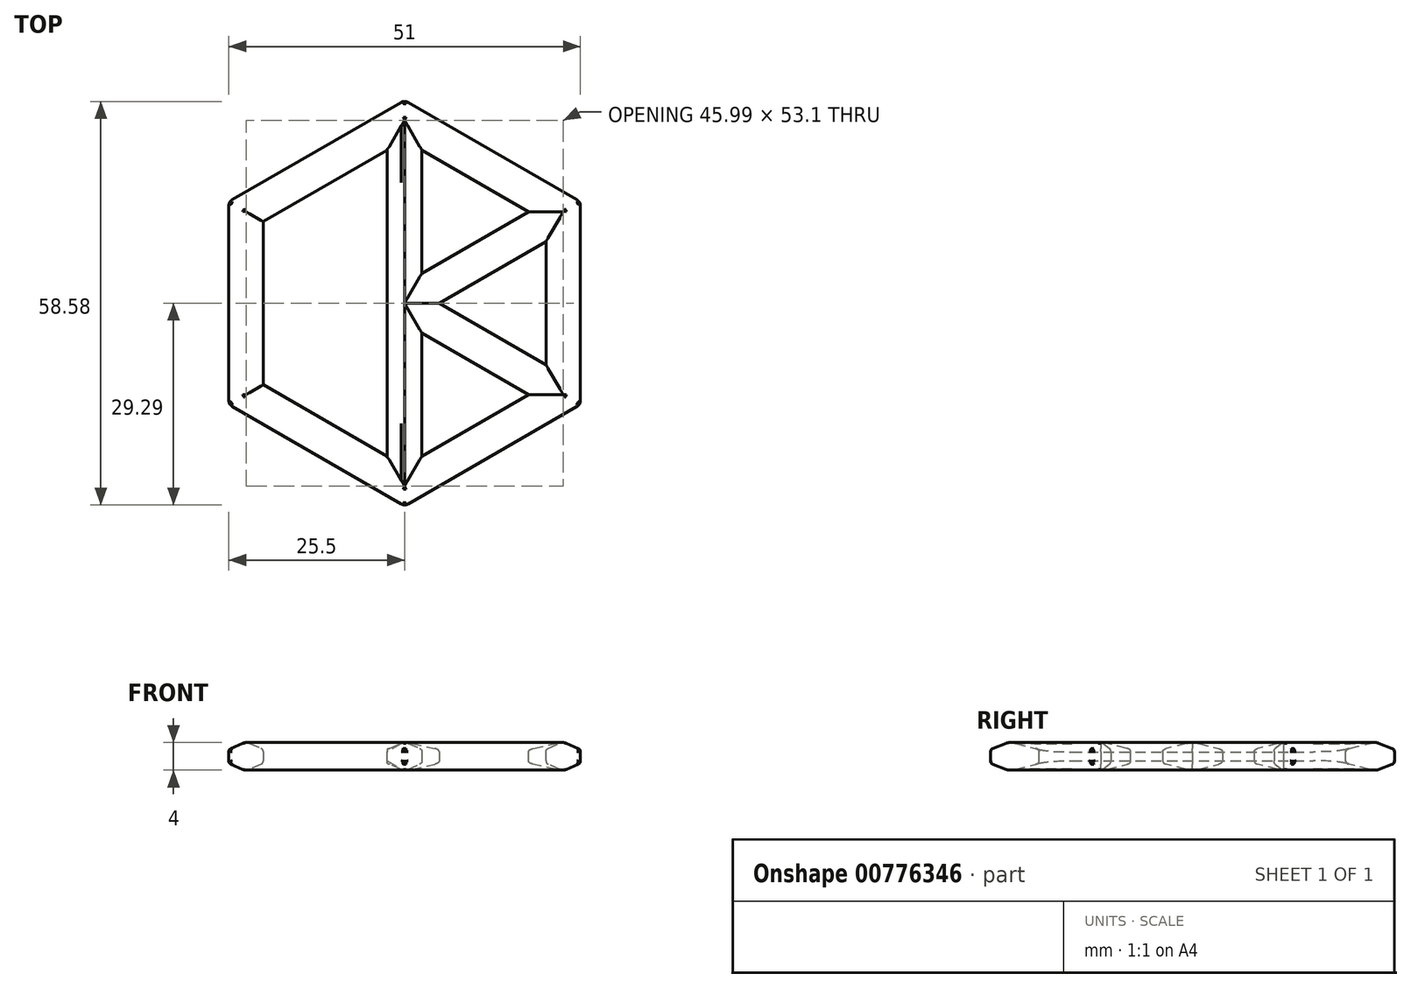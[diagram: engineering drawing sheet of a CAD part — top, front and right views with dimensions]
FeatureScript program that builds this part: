
annotation { "Feature Type Name" : "Feature", "Feature Type Description" : "" }
export const myFeature = defineFeature(function(context is Context, id is Id, definition is map)
    precondition{}
    {
        {
            var Q0;
            Q0=qCreatedBy(makeId("Top.planeOp"),FACE);
            var sketch = newSketch(context, id + "F0", { "sketchPlane" : qUnion([Q0])});
            skCircle(sketch, "E0.cCircle", {"center": v(0, 0) * mm, "radius": 25.5 * mm, "construction": true});
            skLineSegment(sketch, "E0.0", {"start": v(-25.5, -14.72) * mm, "end": v(-25.5, 14.72) * mm});
            skLineSegment(sketch, "E0.1", {"start": v(-25.5, 14.72) * mm, "end": v(0, 29.44) * mm});
            skLineSegment(sketch, "E0.2", {"start": v(0, 29.44) * mm, "end": v(25.5, 14.72) * mm});
            skLineSegment(sketch, "E0.3", {"start": v(25.5, 14.72) * mm, "end": v(25.5, -14.72) * mm});
            skLineSegment(sketch, "E0.4", {"start": v(25.5, -14.72) * mm, "end": v(0, -29.44) * mm});
            skLineSegment(sketch, "E0.5", {"start": v(0, -29.44) * mm, "end": v(-25.5, -14.72) * mm});
            skPoint(sketch, "E0.0.midPoint", {"position": v(-25.5, 0) * mm});
            skSolve(sketch);
        }
        {
            var Q0;
            Q0=qCreatedBy(makeId("Front.planeOp"),FACE);
            var sketch = newSketch(context, id + "F1", { "sketchPlane" : qUnion([Q0])});
            skLineSegment(sketch, "E1", {"start": v(-25.5, -1) * mm, "end": v(-25.5, 1) * mm});
            skLineSegment(sketch, "E2", {"start": v(-22.75, 2) * mm, "end": v(-20.5, 1) * mm});
            skLineSegment(sketch, "E3", {"start": v(-20.5, 1) * mm, "end": v(-20.5, -1) * mm});
            skLineSegment(sketch, "E4", {"start": v(-20.5, -1) * mm, "end": v(-22.75, -2) * mm});
            skLineSegment(sketch, "E5", {"start": v(-23.25, 2) * mm, "end": v(-23.25, -2) * mm});
            skLineSegment(sketch, "E6", {"start": v(-22.75, -2) * mm, "end": v(-22.75, 2) * mm});
            skLineSegment(sketch, "E7", {"start": v(-25.5, -1) * mm, "end": v(-23.25, -2) * mm});
            skLineSegment(sketch, "E8", {"start": v(-22.75, -2) * mm, "end": v(-23.25, -2) * mm});
            skLineSegment(sketch, "E9", {"start": v(-23.25, 2) * mm, "end": v(-22.75, 2) * mm});
            skLineSegment(sketch, "E10", {"start": v(-25.5, 1) * mm, "end": v(-23.25, 2) * mm});
            skLineSegment(sketch, "E11", {"start": v(-22.75, 2) * mm, "end": v(-23.25, -2) * mm});
            skPoint(sketch, "E12", {"position": v(-23, 0) * mm});
            skSolve(sketch);
        }
        {
            var Q0;
            Q0=makeQuery(id+"F1.imprint","IMPRINT",FACE,{"disambiguationData":[TD([[makeQuery(id+"F1.imprint","IMPRINT",EDGE,{"derivedFrom":sQuery(id+"F1.wireOp",EDGE,"E1")}),-1.0]])]});
            var Q1;
            Q1=makeQuery(id+"F1.imprint","IMPRINT",FACE,{"disambiguationData":[TD([[makeQuery(id+"F1.imprint","IMPRINT",EDGE,{"derivedFrom":sQuery(id+"F1.wireOp",EDGE,"E5")}),1.0]])]});
            var Q2;
            Q2=makeQuery(id+"F1.imprint","IMPRINT",FACE,{"disambiguationData":[TD([[makeQuery(id+"F1.imprint","IMPRINT",EDGE,{"derivedFrom":sQuery(id+"F1.wireOp",EDGE,"E6")}),1.0]])]});
            var Q3;
            Q3=makeQuery(id+"F1.imprint","IMPRINT",FACE,{"disambiguationData":[TD([[makeQuery(id+"F1.imprint","IMPRINT",EDGE,{"derivedFrom":sQuery(id+"F1.wireOp",EDGE,"E2")}),-1.0]])]});
            var Q4;
            Q4=sQuery(id+"F0.wireOp",EDGE,"E0.3");
            var Q5;
            Q5=sQuery(id+"F0.wireOp",EDGE,"E0.2");
            var Q6;
            Q6=sQuery(id+"F0.wireOp",EDGE,"E0.1");
            var Q7;
            Q7=sQuery(id+"F0.wireOp",EDGE,"E0.0");
            var Q8;
            Q8=sQuery(id+"F0.wireOp",EDGE,"E0.5");
            var Q9;
            Q9=sQuery(id+"F0.wireOp",EDGE,"E0.4");
            sweep(context, id + "F2", {"profiles" : qUnion([Q0, Q1, Q2, Q3]), "path" : qUnion([Q4, Q5, Q6, Q7, Q8, Q9])});
        }
        {
            var Q0;
            Q0=qCreatedBy(makeId("Front.planeOp"),FACE);
            var sketch = newSketch(context, id + "F3", { "sketchPlane" : qUnion([Q0])});
            skLineSegment(sketch, "E13", {"start": v(-2.5, -1) * mm, "end": v(-2.5, 1) * mm});
            skLineSegment(sketch, "E14", {"start": v(0.25, 2) * mm, "end": v(2.5, 1) * mm});
            skLineSegment(sketch, "E15", {"start": v(2.5, 1) * mm, "end": v(2.5, -1) * mm});
            skLineSegment(sketch, "E16", {"start": v(2.5, -1) * mm, "end": v(0.25, -2) * mm});
            skLineSegment(sketch, "E17", {"start": v(-0.25, 2) * mm, "end": v(-0.25, -2) * mm});
            skLineSegment(sketch, "E18", {"start": v(0.25, -2) * mm, "end": v(0.25, 2) * mm});
            skLineSegment(sketch, "E19", {"start": v(-2.5, -1) * mm, "end": v(-0.25, -2) * mm});
            skLineSegment(sketch, "E20", {"start": v(0.25, -2) * mm, "end": v(-0.25, -2) * mm});
            skLineSegment(sketch, "E21", {"start": v(-0.25, 2) * mm, "end": v(0.25, 2) * mm});
            skLineSegment(sketch, "E22", {"start": v(-2.5, 1) * mm, "end": v(-0.25, 2) * mm});
            skLineSegment(sketch, "E23", {"start": v(0, 2) * mm, "end": v(0, -2) * mm});
            skPoint(sketch, "E24", {"position": v(0, 0) * mm});
            skSolve(sketch);
        }
        {
            var Q0;
            Q0 = qSketchRegion(id + "F3", true);
            extrude(context, id + "F4", {"entities" : qUnion([Q0]), "endBound" : BoundingType.UP_TO_NEXT, "depth" : 25 * mm, "offsetDistance" : 25 * mm});
        }
        {
            var Q0;
            Q0=makeQuery(id+"F4.opExtrude","SWEPT_BODY",BODY,{"disambiguationData":[OSD([sQuery(id+"F3.wireOp",EDGE,"E13"),sQuery(id+"F3.wireOp",EDGE,"E14"),sQuery(id+"F3.wireOp",EDGE,"E15"),sQuery(id+"F3.wireOp",EDGE,"E16"),sQuery(id+"F3.wireOp",EDGE,"E19"),sQuery(id+"F3.wireOp",EDGE,"E20"),sQuery(id+"F3.wireOp",EDGE,"E21"),sQuery(id+"F3.wireOp",EDGE,"E22")])]});
            var Q1;
            Q1=sQuery(id+"F3.wireOp",EDGE,"E23");
            circularPattern(context, id + "F5", {"operationType" : NewBodyOperationType.ADD, "entities" : qUnion([Q0]), "axis" : qUnion([Q1]), "angle" : 180 * degree, "instanceCount" : 4, "oppositeDirection" : true, "equalSpace" : true});
        }
        {
            var Q0;
            Q0=qCreatedBy(makeId("Top.planeOp"),FACE);
            var sketch = newSketch(context, id + "F6", { "sketchPlane" : qUnion([Q0])});
            skLineSegment(sketch, "E25", {"start": v(-2.5, 22.23) * mm, "end": v(-0.25, 26.13) * mm});
            skLineSegment(sketch, "E26", {"start": v(-0.25, 26.13) * mm, "end": v(-0.25, -26.13) * mm});
            skLineSegment(sketch, "E27", {"start": v(-0.25, -26.13) * mm, "end": v(-2.5, -22.23) * mm});
            skLineSegment(sketch, "E28", {"start": v(-2.5, -22.23) * mm, "end": v(-2.5, 22.23) * mm});
            skSolve(sketch);
        }
        {
            var Q0;
            Q0 = qSketchRegion(id + "F6", true);
            extrude(context, id + "F7", {"entities" : qUnion([Q0]), "operationType" : NewBodyOperationType.REMOVE, "endBound" : BoundingType.SYMMETRIC, "oppositeDirection" : true, "depth" : 5 * mm, "offsetDistance" : 25 * mm});
        }
        {
            var Q0;
            Q0=qCreatedBy(makeId("Front.planeOp"),FACE);
            var sketch = newSketch(context, id + "F8", { "sketchPlane" : qUnion([Q0])});
            skLineSegment(sketch, "E29", {"start": v(-0.25, 2) * mm, "end": v(-2.5, 0.65) * mm});
            skLineSegment(sketch, "E30", {"start": v(-2.5, 0.65) * mm, "end": v(-2.5, -0.65) * mm});
            skLineSegment(sketch, "E31", {"start": v(-2.5, -0.65) * mm, "end": v(-0.25, -2) * mm});
            skLineSegment(sketch, "E32", {"start": v(-0.25, -2) * mm, "end": v(-0.25, 2) * mm});
            skSolve(sketch);
        }
        {
            var Q0;
            Q0 = qSketchRegion(id + "F8", true);
            extrude(context, id + "F9", {"entities" : qUnion([Q0]), "operationType" : NewBodyOperationType.ADD, "endBound" : BoundingType.SYMMETRIC, "depth" : 35 * mm, "offsetDistance" : 25 * mm});
        }
        {
            var Q1;
            Q1=makeQuery(id+"F7.boolean.opBoolean","COPY",FACE,{"derivedFrom":makeQuery(id+"F7.opExtrude","SWEPT_FACE",FACE,{"disambiguationData":[OSD([sQuery(id+"F6.wireOp",EDGE,"E25")])]})});
            var Q2;
            Q2=makeQuery(id+"F9.opExtrude","CAP_FACE",FACE,{"disambiguationData":[OSD([sQuery(id+"F8.wireOp",EDGE,"E29"),sQuery(id+"F8.wireOp",EDGE,"E30"),sQuery(id+"F8.wireOp",EDGE,"E31"),sQuery(id+"F8.wireOp",EDGE,"E32")])],"isStart":true});
            loft(context, id + "F10", {"operationType" : NewBodyOperationType.ADD, "endCondition" : LoftEndDerivativeType.MATCH_TANGENT, "endMagnitude" : 2, "sheetProfilesArray" : [{ "sheetProfileEntities" : qUnion([Q1]) }, { "sheetProfileEntities" : qUnion([Q2]) }]});
        }
        {
            var Q1;
            Q1=makeQuery(id+"F7.boolean.opBoolean","COPY",FACE,{"derivedFrom":makeQuery(id+"F7.opExtrude","SWEPT_FACE",FACE,{"disambiguationData":[OSD([sQuery(id+"F6.wireOp",EDGE,"E27")])]})});
            var Q2;
            Q2=makeQuery(id+"F9.opExtrude","CAP_FACE",FACE,{"disambiguationData":[OSD([sQuery(id+"F8.wireOp",EDGE,"E29"),sQuery(id+"F8.wireOp",EDGE,"E30"),sQuery(id+"F8.wireOp",EDGE,"E31"),sQuery(id+"F8.wireOp",EDGE,"E32")])],"isStart":false});
            loft(context, id + "F11", {"operationType" : NewBodyOperationType.ADD, "endCondition" : LoftEndDerivativeType.MATCH_TANGENT, "endMagnitude" : 2, "sheetProfilesArray" : [{ "sheetProfileEntities" : qUnion([Q1]) }, { "sheetProfileEntities" : qUnion([Q2]) }]});
        }
        {
            var Q0;
            Q0=makeQuery(id+"F2.opSweep","MID_CAP_EDGE",EDGE,{"disambiguationData":[OSD([sQuery(id+"F0.wireOp",VERTEX,"E0.4.start"),sQuery(id+"F1.wireOp",EDGE,"E1")])],"capPos":2.0});
            var Q1;
            Q1=makeQuery(id+"F2.opSweep","MID_CAP_EDGE",EDGE,{"disambiguationData":[OSD([sQuery(id+"F0.wireOp",VERTEX,"E0.4.start"),sQuery(id+"F1.wireOp",EDGE,"E10")])],"capPos":2.0});
            var Q2;
            Q2=makeQuery(id+"F2.opSweep","MID_CAP_EDGE",EDGE,{"disambiguationData":[OSD([sQuery(id+"F0.wireOp",VERTEX,"E0.4.start"),sQuery(id+"F1.wireOp",EDGE,"E7")])],"capPos":2.0});
            var Q3;
            Q3=makeQuery(id+"F2.opSweep","MID_CAP_EDGE",EDGE,{"disambiguationData":[OSD([sQuery(id+"F0.wireOp",VERTEX,"E0.2.end"),sQuery(id+"F1.wireOp",EDGE,"E10")])],"capPos":3.0});
            var Q4;
            Q4=makeQuery(id+"F2.opSweep","MID_CAP_EDGE",EDGE,{"disambiguationData":[OSD([sQuery(id+"F0.wireOp",VERTEX,"E0.2.end"),sQuery(id+"F1.wireOp",EDGE,"E1")])],"capPos":3.0});
            var Q5;
            Q5=makeQuery(id+"F2.opSweep","MID_CAP_EDGE",EDGE,{"disambiguationData":[OSD([sQuery(id+"F0.wireOp",VERTEX,"E0.2.end"),sQuery(id+"F1.wireOp",EDGE,"E7")])],"capPos":3.0});
            var Q6;
            Q6=makeQuery(id+"F2.opSweep","MID_CAP_EDGE",EDGE,{"disambiguationData":[OSD([sQuery(id+"F0.wireOp",VERTEX,"E0.1.end"),sQuery(id+"F1.wireOp",EDGE,"E7")])],"capPos":4.0});
            var Q7;
            Q7=makeQuery(id+"F2.opSweep","MID_CAP_EDGE",EDGE,{"disambiguationData":[OSD([sQuery(id+"F0.wireOp",VERTEX,"E0.1.end"),sQuery(id+"F1.wireOp",EDGE,"E1")])],"capPos":4.0});
            var Q8;
            Q8=makeQuery(id+"F2.opSweep","MID_CAP_EDGE",EDGE,{"disambiguationData":[OSD([sQuery(id+"F0.wireOp",VERTEX,"E0.1.end"),sQuery(id+"F1.wireOp",EDGE,"E10")])],"capPos":4.0});
            var Q9;
            Q9=makeQuery(id+"F2.opSweep","MID_CAP_EDGE",EDGE,{"disambiguationData":[OSD([sQuery(id+"F0.wireOp",VERTEX,"E0.0.end"),sQuery(id+"F1.wireOp",EDGE,"E1")])],"capPos":5.0});
            var Q10;
            Q10=makeQuery(id+"F2.opSweep","MID_CAP_EDGE",EDGE,{"disambiguationData":[OSD([sQuery(id+"F0.wireOp",VERTEX,"E0.0.end"),sQuery(id+"F1.wireOp",EDGE,"E10")])],"capPos":5.0});
            var Q11;
            Q11=makeQuery(id+"F2.opSweep","MID_CAP_EDGE",EDGE,{"disambiguationData":[OSD([sQuery(id+"F0.wireOp",VERTEX,"E0.0.end"),sQuery(id+"F1.wireOp",EDGE,"E7")])],"capPos":5.0});
            var Q12;
            Q12=makeQuery(id+"F2.opSweep","CAP_EDGE",EDGE,{"disambiguationData":[OSD([sQuery(id+"F0.wireOp",VERTEX,"E0.5.end"),sQuery(id+"F1.wireOp",EDGE,"E7")])],"isStart":true});
            var Q13;
            Q13=makeQuery(id+"F2.opSweep","CAP_EDGE",EDGE,{"disambiguationData":[OSD([sQuery(id+"F0.wireOp",VERTEX,"E0.5.end"),sQuery(id+"F1.wireOp",EDGE,"E1")])],"isStart":true});
            var Q14;
            Q14=makeQuery(id+"F2.opSweep","CAP_EDGE",EDGE,{"disambiguationData":[OSD([sQuery(id+"F0.wireOp",VERTEX,"E0.5.end"),sQuery(id+"F1.wireOp",EDGE,"E10")])],"isStart":true});
            var Q15;
            Q15=makeQuery(id+"F2.opSweep","MID_CAP_EDGE",EDGE,{"disambiguationData":[OSD([sQuery(id+"F0.wireOp",VERTEX,"E0.4.end"),sQuery(id+"F1.wireOp",EDGE,"E10")])],"capPos":1.0});
            var Q16;
            Q16=makeQuery(id+"F2.opSweep","MID_CAP_EDGE",EDGE,{"disambiguationData":[OSD([sQuery(id+"F0.wireOp",VERTEX,"E0.4.end"),sQuery(id+"F1.wireOp",EDGE,"E1")])],"capPos":1.0});
            var Q17;
            Q17=makeQuery(id+"F2.opSweep","MID_CAP_EDGE",EDGE,{"disambiguationData":[OSD([sQuery(id+"F0.wireOp",VERTEX,"E0.4.end"),sQuery(id+"F1.wireOp",EDGE,"E7")])],"capPos":1.0});
            fillet(context, id + "F12", {"entities" : qUnion([Q0, Q1, Q2, Q3, Q4, Q5, Q6, Q7, Q8, Q9, Q10, Q11, Q12, Q13, Q14, Q15, Q16, Q17]), "radius" : 1 * mm, "tangentPropagation" : true, "allowEdgeOverflow" : false});
        }
        {
            var Q0;
            Q0=makeQuery(id+"F2.opSweep","SWEPT_EDGE",EDGE,{"disambiguationData":[OSD([sQuery(id+"F0.wireOp",EDGE,"E0.2"),sQuery(id+"F1.wireOp",EDGE,"E1"),sQuery(id+"F1.wireOp",EDGE,"E10")])]});
            var Q1;
            Q1=makeQuery(id+"F2.opSweep","SWEPT_EDGE",EDGE,{"disambiguationData":[OSD([sQuery(id+"F0.wireOp",EDGE,"E0.1"),sQuery(id+"F1.wireOp",EDGE,"E1"),sQuery(id+"F1.wireOp",EDGE,"E10")])]});
            var Q2;
            Q2=makeQuery(id+"F2.opSweep","SWEPT_EDGE",EDGE,{"disambiguationData":[OSD([sQuery(id+"F0.wireOp",EDGE,"E0.0"),sQuery(id+"F1.wireOp",EDGE,"E1"),sQuery(id+"F1.wireOp",EDGE,"E10")])]});
            var Q3;
            Q3=makeQuery(id+"F2.opSweep","SWEPT_EDGE",EDGE,{"disambiguationData":[OSD([sQuery(id+"F0.wireOp",EDGE,"E0.5"),sQuery(id+"F1.wireOp",EDGE,"E1"),sQuery(id+"F1.wireOp",EDGE,"E10")])]});
            var Q4;
            Q4=makeQuery(id+"F2.opSweep","SWEPT_EDGE",EDGE,{"disambiguationData":[OSD([sQuery(id+"F0.wireOp",EDGE,"E0.1"),sQuery(id+"F1.wireOp",EDGE,"E1"),sQuery(id+"F1.wireOp",EDGE,"E7")])]});
            var Q5;
            Q5=makeQuery(id+"F2.opSweep","SWEPT_EDGE",EDGE,{"disambiguationData":[OSD([sQuery(id+"F0.wireOp",EDGE,"E0.0"),sQuery(id+"F1.wireOp",EDGE,"E1"),sQuery(id+"F1.wireOp",EDGE,"E7")])]});
            var Q6;
            Q6=makeQuery(id+"F2.opSweep","SWEPT_EDGE",EDGE,{"disambiguationData":[OSD([sQuery(id+"F0.wireOp",EDGE,"E0.5"),sQuery(id+"F1.wireOp",EDGE,"E1"),sQuery(id+"F1.wireOp",EDGE,"E7")])]});
            var Q7;
            Q7=makeQuery(id+"F2.opSweep","SWEPT_EDGE",EDGE,{"disambiguationData":[OSD([sQuery(id+"F0.wireOp",EDGE,"E0.4"),sQuery(id+"F1.wireOp",EDGE,"E1"),sQuery(id+"F1.wireOp",EDGE,"E10")])]});
            var Q8;
            Q8=makeQuery(id+"F2.opSweep","SWEPT_EDGE",EDGE,{"disambiguationData":[OSD([sQuery(id+"F0.wireOp",EDGE,"E0.3"),sQuery(id+"F1.wireOp",EDGE,"E1"),sQuery(id+"F1.wireOp",EDGE,"E10")])]});
            var Q9;
            Q9=makeQuery(id+"F2.opSweep","SWEPT_EDGE",EDGE,{"disambiguationData":[OSD([sQuery(id+"F0.wireOp",EDGE,"E0.4"),sQuery(id+"F1.wireOp",EDGE,"E1"),sQuery(id+"F1.wireOp",EDGE,"E7")])]});
            var Q10;
            Q10=makeQuery(id+"F2.opSweep","SWEPT_EDGE",EDGE,{"disambiguationData":[OSD([sQuery(id+"F0.wireOp",EDGE,"E0.3"),sQuery(id+"F1.wireOp",EDGE,"E1"),sQuery(id+"F1.wireOp",EDGE,"E7")])]});
            var Q11;
            Q11=makeQuery(id+"F2.opSweep","SWEPT_EDGE",EDGE,{"disambiguationData":[OSD([sQuery(id+"F0.wireOp",EDGE,"E0.2"),sQuery(id+"F1.wireOp",EDGE,"E1"),sQuery(id+"F1.wireOp",EDGE,"E7")])]});
            var Q12;
            Q12=makeQuery(id+"F5.opPattern","COPY",EDGE,{"derivedFrom":makeQuery(id+"F4.opExtrude","SWEPT_EDGE",EDGE,{"disambiguationData":[OSD([sQuery(id+"F3.wireOp",EDGE,"E13"),sQuery(id+"F3.wireOp",EDGE,"E19")])]}),"instanceName":"3"});
            var Q13;
            Q13=makeQuery(id+"F5.opPattern","COPY",EDGE,{"derivedFrom":makeQuery(id+"F4.opExtrude","SWEPT_EDGE",EDGE,{"disambiguationData":[OSD([sQuery(id+"F3.wireOp",EDGE,"E13"),sQuery(id+"F3.wireOp",EDGE,"E22")])]}),"instanceName":"3"});
            var Q14;
            Q14=makeQuery(id+"F5.opPattern","COPY",EDGE,{"derivedFrom":makeQuery(id+"F4.opExtrude","SWEPT_EDGE",EDGE,{"disambiguationData":[OSD([sQuery(id+"F3.wireOp",EDGE,"E15"),sQuery(id+"F3.wireOp",EDGE,"E16")])]}),"instanceName":"1"});
            var Q15;
            Q15=makeQuery(id+"F5.opPattern","COPY",EDGE,{"derivedFrom":makeQuery(id+"F4.opExtrude","SWEPT_EDGE",EDGE,{"disambiguationData":[OSD([sQuery(id+"F3.wireOp",EDGE,"E14"),sQuery(id+"F3.wireOp",EDGE,"E15")])]}),"instanceName":"1"});
            var Q16;
            Q16=makeQuery(id+"F4.opExtrude","SWEPT_EDGE",EDGE,{"disambiguationData":[OSD([sQuery(id+"F3.wireOp",EDGE,"E15"),sQuery(id+"F3.wireOp",EDGE,"E16")])]});
            var Q17;
            Q17=makeQuery(id+"F2.opSweep","SWEPT_EDGE",EDGE,{"disambiguationData":[OSD([sQuery(id+"F0.wireOp",EDGE,"E0.4"),sQuery(id+"F1.wireOp",EDGE,"E3"),sQuery(id+"F1.wireOp",EDGE,"E4")])]});
            var Q18;
            Q18=makeQuery(id+"F2.opSweep","SWEPT_EDGE",EDGE,{"disambiguationData":[OSD([sQuery(id+"F0.wireOp",EDGE,"E0.4"),sQuery(id+"F1.wireOp",EDGE,"E2"),sQuery(id+"F1.wireOp",EDGE,"E3")])]});
            var Q19;
            Q19=makeQuery(id+"F4.opExtrude","SWEPT_EDGE",EDGE,{"disambiguationData":[OSD([sQuery(id+"F3.wireOp",EDGE,"E14"),sQuery(id+"F3.wireOp",EDGE,"E15")])]});
            var Q20;
            Q20=makeQuery(id+"F5.opPattern","COPY",EDGE,{"derivedFrom":makeQuery(id+"F4.opExtrude","SWEPT_EDGE",EDGE,{"disambiguationData":[OSD([sQuery(id+"F3.wireOp",EDGE,"E15"),sQuery(id+"F3.wireOp",EDGE,"E16")])]}),"instanceName":"2"});
            var Q21;
            Q21=makeQuery(id+"F5.opPattern","COPY",EDGE,{"derivedFrom":makeQuery(id+"F4.opExtrude","SWEPT_EDGE",EDGE,{"disambiguationData":[OSD([sQuery(id+"F3.wireOp",EDGE,"E14"),sQuery(id+"F3.wireOp",EDGE,"E15")])]}),"instanceName":"2"});
            var Q22;
            Q22=makeQuery(id+"F2.opSweep","SWEPT_EDGE",EDGE,{"disambiguationData":[OSD([sQuery(id+"F0.wireOp",EDGE,"E0.3"),sQuery(id+"F1.wireOp",EDGE,"E3"),sQuery(id+"F1.wireOp",EDGE,"E4")])]});
            var Q23;
            Q23=makeQuery(id+"F2.opSweep","SWEPT_EDGE",EDGE,{"disambiguationData":[OSD([sQuery(id+"F0.wireOp",EDGE,"E0.3"),sQuery(id+"F1.wireOp",EDGE,"E2"),sQuery(id+"F1.wireOp",EDGE,"E3")])]});
            var Q24;
            Q24=makeQuery(id+"F5.opPattern","COPY",EDGE,{"derivedFrom":makeQuery(id+"F4.opExtrude","SWEPT_EDGE",EDGE,{"disambiguationData":[OSD([sQuery(id+"F3.wireOp",EDGE,"E13"),sQuery(id+"F3.wireOp",EDGE,"E19")])]}),"instanceName":"1"});
            var Q25;
            Q25=makeQuery(id+"F5.opPattern","COPY",EDGE,{"derivedFrom":makeQuery(id+"F4.opExtrude","SWEPT_EDGE",EDGE,{"disambiguationData":[OSD([sQuery(id+"F3.wireOp",EDGE,"E13"),sQuery(id+"F3.wireOp",EDGE,"E22")])]}),"instanceName":"1"});
            var Q26;
            Q26=makeQuery(id+"F5.opPattern","COPY",EDGE,{"derivedFrom":makeQuery(id+"F4.opExtrude","SWEPT_EDGE",EDGE,{"disambiguationData":[OSD([sQuery(id+"F3.wireOp",EDGE,"E13"),sQuery(id+"F3.wireOp",EDGE,"E22")])]}),"instanceName":"2"});
            var Q27;
            Q27=makeQuery(id+"F5.opPattern","COPY",EDGE,{"derivedFrom":makeQuery(id+"F4.opExtrude","SWEPT_EDGE",EDGE,{"disambiguationData":[OSD([sQuery(id+"F3.wireOp",EDGE,"E13"),sQuery(id+"F3.wireOp",EDGE,"E19")])]}),"instanceName":"2"});
            var Q28;
            Q28=makeQuery(id+"F2.opSweep","SWEPT_EDGE",EDGE,{"disambiguationData":[OSD([sQuery(id+"F0.wireOp",EDGE,"E0.2"),sQuery(id+"F1.wireOp",EDGE,"E3"),sQuery(id+"F1.wireOp",EDGE,"E4")])]});
            var Q29;
            Q29=makeQuery(id+"F2.opSweep","SWEPT_EDGE",EDGE,{"disambiguationData":[OSD([sQuery(id+"F0.wireOp",EDGE,"E0.2"),sQuery(id+"F1.wireOp",EDGE,"E2"),sQuery(id+"F1.wireOp",EDGE,"E3")])]});
            var Q30;
            Q30=makeQuery(id+"F2.opSweep","SWEPT_EDGE",EDGE,{"disambiguationData":[OSD([sQuery(id+"F0.wireOp",EDGE,"E0.0"),sQuery(id+"F1.wireOp",EDGE,"E2"),sQuery(id+"F1.wireOp",EDGE,"E3")])]});
            var Q31;
            Q31=makeQuery(id+"F2.opSweep","SWEPT_EDGE",EDGE,{"disambiguationData":[OSD([sQuery(id+"F0.wireOp",EDGE,"E0.1"),sQuery(id+"F1.wireOp",EDGE,"E2"),sQuery(id+"F1.wireOp",EDGE,"E3")])]});
            var Q32;
            Q32=makeQuery(id+"F2.opSweep","SWEPT_EDGE",EDGE,{"disambiguationData":[OSD([sQuery(id+"F0.wireOp",EDGE,"E0.5"),sQuery(id+"F1.wireOp",EDGE,"E2"),sQuery(id+"F1.wireOp",EDGE,"E3")])]});
            var Q33;
            Q33=makeQuery(id+"F2.opSweep","SWEPT_EDGE",EDGE,{"disambiguationData":[OSD([sQuery(id+"F0.wireOp",EDGE,"E0.5"),sQuery(id+"F1.wireOp",EDGE,"E3"),sQuery(id+"F1.wireOp",EDGE,"E4")])]});
            var Q34;
            Q34=makeQuery(id+"F2.opSweep","SWEPT_EDGE",EDGE,{"disambiguationData":[OSD([sQuery(id+"F0.wireOp",EDGE,"E0.0"),sQuery(id+"F1.wireOp",EDGE,"E3"),sQuery(id+"F1.wireOp",EDGE,"E4")])]});
            var Q35;
            Q35=makeQuery(id+"F2.opSweep","SWEPT_EDGE",EDGE,{"disambiguationData":[OSD([sQuery(id+"F0.wireOp",EDGE,"E0.1"),sQuery(id+"F1.wireOp",EDGE,"E3"),sQuery(id+"F1.wireOp",EDGE,"E4")])]});
            fillet(context, id + "F13", {"entities" : qUnion([Q0, Q1, Q2, Q3, Q4, Q5, Q6, Q7, Q8, Q9, Q10, Q11, Q12, Q13, Q14, Q15, Q16, Q17, Q18, Q19, Q20, Q21, Q22, Q23, Q24, Q25, Q26, Q27, Q28, Q29, Q30, Q31, Q32, Q33, Q34, Q35]), "radius" : .5 * mm, "tangentPropagation" : true, "allowEdgeOverflow" : false});
        }
        {
            var Q0;
            Q0=makeQuery(id+"F2.opSweep","SWEPT_EDGE",EDGE,{"disambiguationData":[OSD([sQuery(id+"F0.wireOp",EDGE,"E0.1"),sQuery(id+"F1.wireOp",EDGE,"E2"),sQuery(id+"F1.wireOp",EDGE,"E6"),sQuery(id+"F1.wireOp",EDGE,"E9"),sQuery(id+"F1.wireOp",EDGE,"E11")])]});
            var Q1;
            {var subQ0=sQuery(id+"F8.wireOp",EDGE,"E32");var subQ1=sQuery(id+"F8.wireOp",EDGE,"E29");var subQ2=sQuery(id+"F3.wireOp",EDGE,"E21");var subQ3=sQuery(id+"F3.wireOp",EDGE,"E14");var subQ15=sQuery(id+"F3.wireOp",EDGE,"E22");var subQ16=makeQuery(id+"F5.boolean.opBoolean","MERGE",EDGE,{"derivedFrom":[makeQuery(id+"F4.opExtrude","SWEPT_EDGE",EDGE,{"disambiguationData":[OSD([sQuery(id+"F3.wireOp",EDGE,"E17"),subQ2,subQ15])]}),makeQuery(id+"F5.opPattern","COPY",EDGE,{"derivedFrom":makeQuery(id+"F4.opExtrude","SWEPT_EDGE",EDGE,{"disambiguationData":[OSD([subQ3,sQuery(id+"F3.wireOp",EDGE,"E18"),subQ2])]}),"instanceName":"3"})]});Q1=qUnion([makeQuery(id+"F9.boolean.opBoolean","MERGE",EDGE,{"derivedFrom":[subQ16,makeQuery(id+"F9.opExtrude","SWEPT_EDGE",EDGE,{"disambiguationData":[OSD([subQ1,subQ0])]})]}),makeQuery(id+"F11.boolean.opBoolean","MERGE",EDGE,{"derivedFrom":[makeQuery(id+"F9.boolean.opBoolean","SPLIT",EDGE,{"disambiguationData":[TD([makeQuery(id+"F7.boolean.opBoolean","COPY",FACE,{"derivedFrom":makeQuery(id+"F7.opExtrude","SWEPT_FACE",FACE,{"disambiguationData":[OSD([sQuery(id+"F6.wireOp",EDGE,"E27")])]})})])],"derivedFrom":subQ16}),makeQuery(id+"F11.opLoft","SWEPT_EDGE",EDGE,{"disambiguationData":[OSD([subQ2,subQ15,subQ1,subQ0])]})]}),makeQuery(id+"F10.boolean.opBoolean","MERGE",EDGE,{"derivedFrom":[makeQuery(id+"F9.boolean.opBoolean","SPLIT",EDGE,{"disambiguationData":[TD([makeQuery(id+"F7.boolean.opBoolean","COPY",FACE,{"derivedFrom":makeQuery(id+"F7.opExtrude","SWEPT_FACE",FACE,{"disambiguationData":[OSD([sQuery(id+"F6.wireOp",EDGE,"E25")])]})})])],"derivedFrom":subQ16}),makeQuery(id+"F10.opLoft","SWEPT_EDGE",EDGE,{"disambiguationData":[OSD([subQ3,subQ2,subQ1,subQ0])]})]})]);}
            var Q2;
            Q2=makeQuery(id+"F2.opSweep","SWEPT_EDGE",EDGE,{"disambiguationData":[OSD([sQuery(id+"F0.wireOp",EDGE,"E0.5"),sQuery(id+"F1.wireOp",EDGE,"E2"),sQuery(id+"F1.wireOp",EDGE,"E6"),sQuery(id+"F1.wireOp",EDGE,"E9"),sQuery(id+"F1.wireOp",EDGE,"E11")])]});
            var Q3;
            Q3=makeQuery(id+"F4.opExtrude","SWEPT_EDGE",EDGE,{"disambiguationData":[OSD([sQuery(id+"F3.wireOp",EDGE,"E14"),sQuery(id+"F3.wireOp",EDGE,"E18"),sQuery(id+"F3.wireOp",EDGE,"E21")])]});
            var Q4;
            Q4=makeQuery(id+"F2.opSweep","SWEPT_EDGE",EDGE,{"disambiguationData":[OSD([sQuery(id+"F0.wireOp",EDGE,"E0.4"),sQuery(id+"F1.wireOp",EDGE,"E2"),sQuery(id+"F1.wireOp",EDGE,"E6"),sQuery(id+"F1.wireOp",EDGE,"E9"),sQuery(id+"F1.wireOp",EDGE,"E11")])]});
            var Q5;
            Q5=makeQuery(id+"F5.opPattern","COPY",EDGE,{"derivedFrom":makeQuery(id+"F4.opExtrude","SWEPT_EDGE",EDGE,{"disambiguationData":[OSD([sQuery(id+"F3.wireOp",EDGE,"E17"),sQuery(id+"F3.wireOp",EDGE,"E21"),sQuery(id+"F3.wireOp",EDGE,"E22")])]}),"instanceName":"1"});
            var Q6;
            Q6=makeQuery(id+"F5.opPattern","COPY",EDGE,{"derivedFrom":makeQuery(id+"F4.opExtrude","SWEPT_EDGE",EDGE,{"disambiguationData":[OSD([sQuery(id+"F3.wireOp",EDGE,"E14"),sQuery(id+"F3.wireOp",EDGE,"E18"),sQuery(id+"F3.wireOp",EDGE,"E21")])]}),"instanceName":"1"});
            var Q7;
            Q7=makeQuery(id+"F5.opPattern","COPY",EDGE,{"derivedFrom":makeQuery(id+"F4.opExtrude","SWEPT_EDGE",EDGE,{"disambiguationData":[OSD([sQuery(id+"F3.wireOp",EDGE,"E17"),sQuery(id+"F3.wireOp",EDGE,"E21"),sQuery(id+"F3.wireOp",EDGE,"E22")])]}),"instanceName":"2"});
            var Q8;
            Q8=makeQuery(id+"F5.opPattern","COPY",EDGE,{"derivedFrom":makeQuery(id+"F4.opExtrude","SWEPT_EDGE",EDGE,{"disambiguationData":[OSD([sQuery(id+"F3.wireOp",EDGE,"E17"),sQuery(id+"F3.wireOp",EDGE,"E21"),sQuery(id+"F3.wireOp",EDGE,"E22")])]}),"instanceName":"3"});
            var Q9;
            Q9=makeQuery(id+"F5.opPattern","COPY",EDGE,{"derivedFrom":makeQuery(id+"F4.opExtrude","SWEPT_EDGE",EDGE,{"disambiguationData":[OSD([sQuery(id+"F3.wireOp",EDGE,"E14"),sQuery(id+"F3.wireOp",EDGE,"E18"),sQuery(id+"F3.wireOp",EDGE,"E21")])]}),"instanceName":"2"});
            var Q10;
            Q10=makeQuery(id+"F2.opSweep","SWEPT_EDGE",EDGE,{"disambiguationData":[OSD([sQuery(id+"F0.wireOp",EDGE,"E0.2"),sQuery(id+"F1.wireOp",EDGE,"E2"),sQuery(id+"F1.wireOp",EDGE,"E6"),sQuery(id+"F1.wireOp",EDGE,"E9"),sQuery(id+"F1.wireOp",EDGE,"E11")])]});
            var Q11;
            Q11=makeQuery(id+"F2.opSweep","SWEPT_EDGE",EDGE,{"disambiguationData":[OSD([sQuery(id+"F0.wireOp",EDGE,"E0.0"),sQuery(id+"F1.wireOp",EDGE,"E2"),sQuery(id+"F1.wireOp",EDGE,"E6"),sQuery(id+"F1.wireOp",EDGE,"E9"),sQuery(id+"F1.wireOp",EDGE,"E11")])]});
            var Q12;
            Q12=makeQuery(id+"F2.opSweep","SWEPT_EDGE",EDGE,{"disambiguationData":[OSD([sQuery(id+"F0.wireOp",EDGE,"E0.4"),sQuery(id+"F1.wireOp",EDGE,"E5"),sQuery(id+"F1.wireOp",EDGE,"E9"),sQuery(id+"F1.wireOp",EDGE,"E10")])]});
            var Q13;
            Q13=makeQuery(id+"F2.opSweep","SWEPT_EDGE",EDGE,{"disambiguationData":[OSD([sQuery(id+"F0.wireOp",EDGE,"E0.5"),sQuery(id+"F1.wireOp",EDGE,"E5"),sQuery(id+"F1.wireOp",EDGE,"E9"),sQuery(id+"F1.wireOp",EDGE,"E10")])]});
            var Q14;
            Q14=makeQuery(id+"F2.opSweep","SWEPT_EDGE",EDGE,{"disambiguationData":[OSD([sQuery(id+"F0.wireOp",EDGE,"E0.0"),sQuery(id+"F1.wireOp",EDGE,"E5"),sQuery(id+"F1.wireOp",EDGE,"E9"),sQuery(id+"F1.wireOp",EDGE,"E10")])]});
            var Q15;
            Q15=makeQuery(id+"F2.opSweep","SWEPT_EDGE",EDGE,{"disambiguationData":[OSD([sQuery(id+"F0.wireOp",EDGE,"E0.1"),sQuery(id+"F1.wireOp",EDGE,"E5"),sQuery(id+"F1.wireOp",EDGE,"E9"),sQuery(id+"F1.wireOp",EDGE,"E10")])]});
            var Q16;
            Q16=makeQuery(id+"F2.opSweep","SWEPT_EDGE",EDGE,{"disambiguationData":[OSD([sQuery(id+"F0.wireOp",EDGE,"E0.2"),sQuery(id+"F1.wireOp",EDGE,"E5"),sQuery(id+"F1.wireOp",EDGE,"E9"),sQuery(id+"F1.wireOp",EDGE,"E10")])]});
            var Q17;
            Q17=makeQuery(id+"F2.opSweep","SWEPT_EDGE",EDGE,{"disambiguationData":[OSD([sQuery(id+"F0.wireOp",EDGE,"E0.3"),sQuery(id+"F1.wireOp",EDGE,"E2"),sQuery(id+"F1.wireOp",EDGE,"E6"),sQuery(id+"F1.wireOp",EDGE,"E9"),sQuery(id+"F1.wireOp",EDGE,"E11")])]});
            var Q18;
            Q18=makeQuery(id+"F2.opSweep","SWEPT_EDGE",EDGE,{"disambiguationData":[OSD([sQuery(id+"F0.wireOp",EDGE,"E0.3"),sQuery(id+"F1.wireOp",EDGE,"E5"),sQuery(id+"F1.wireOp",EDGE,"E9"),sQuery(id+"F1.wireOp",EDGE,"E10")])]});
            var Q19;
            Q19=makeQuery(id+"F2.opSweep","SWEPT_EDGE",EDGE,{"disambiguationData":[OSD([sQuery(id+"F0.wireOp",EDGE,"E0.0"),sQuery(id+"F1.wireOp",EDGE,"E5"),sQuery(id+"F1.wireOp",EDGE,"E7"),sQuery(id+"F1.wireOp",EDGE,"E8"),sQuery(id+"F1.wireOp",EDGE,"E11")])]});
            var Q20;
            Q20=makeQuery(id+"F2.opSweep","SWEPT_EDGE",EDGE,{"disambiguationData":[OSD([sQuery(id+"F0.wireOp",EDGE,"E0.1"),sQuery(id+"F1.wireOp",EDGE,"E5"),sQuery(id+"F1.wireOp",EDGE,"E7"),sQuery(id+"F1.wireOp",EDGE,"E8"),sQuery(id+"F1.wireOp",EDGE,"E11")])]});
            var Q21;
            Q21=makeQuery(id+"F2.opSweep","SWEPT_EDGE",EDGE,{"disambiguationData":[OSD([sQuery(id+"F0.wireOp",EDGE,"E0.1"),sQuery(id+"F1.wireOp",EDGE,"E4"),sQuery(id+"F1.wireOp",EDGE,"E6"),sQuery(id+"F1.wireOp",EDGE,"E8")])]});
            var Q22;
            Q22=makeQuery(id+"F2.opSweep","SWEPT_EDGE",EDGE,{"disambiguationData":[OSD([sQuery(id+"F0.wireOp",EDGE,"E0.0"),sQuery(id+"F1.wireOp",EDGE,"E4"),sQuery(id+"F1.wireOp",EDGE,"E6"),sQuery(id+"F1.wireOp",EDGE,"E8")])]});
            var Q23;
            Q23=makeQuery(id+"F2.opSweep","SWEPT_EDGE",EDGE,{"disambiguationData":[OSD([sQuery(id+"F0.wireOp",EDGE,"E0.5"),sQuery(id+"F1.wireOp",EDGE,"E4"),sQuery(id+"F1.wireOp",EDGE,"E6"),sQuery(id+"F1.wireOp",EDGE,"E8")])]});
            var Q24;
            Q24=makeQuery(id+"F2.opSweep","SWEPT_EDGE",EDGE,{"disambiguationData":[OSD([sQuery(id+"F0.wireOp",EDGE,"E0.5"),sQuery(id+"F1.wireOp",EDGE,"E5"),sQuery(id+"F1.wireOp",EDGE,"E7"),sQuery(id+"F1.wireOp",EDGE,"E8"),sQuery(id+"F1.wireOp",EDGE,"E11")])]});
            var Q25;
            Q25=makeQuery(id+"F2.opSweep","SWEPT_EDGE",EDGE,{"disambiguationData":[OSD([sQuery(id+"F0.wireOp",EDGE,"E0.2"),sQuery(id+"F1.wireOp",EDGE,"E5"),sQuery(id+"F1.wireOp",EDGE,"E7"),sQuery(id+"F1.wireOp",EDGE,"E8"),sQuery(id+"F1.wireOp",EDGE,"E11")])]});
            var Q26;
            Q26=makeQuery(id+"F2.opSweep","SWEPT_EDGE",EDGE,{"disambiguationData":[OSD([sQuery(id+"F0.wireOp",EDGE,"E0.2"),sQuery(id+"F1.wireOp",EDGE,"E4"),sQuery(id+"F1.wireOp",EDGE,"E6"),sQuery(id+"F1.wireOp",EDGE,"E8")])]});
            var Q27;
            {var subQ0=sQuery(id+"F8.wireOp",EDGE,"E32");var subQ1=sQuery(id+"F8.wireOp",EDGE,"E31");var subQ2=sQuery(id+"F3.wireOp",EDGE,"E20");var subQ3=sQuery(id+"F3.wireOp",EDGE,"E19");var subQ15=sQuery(id+"F3.wireOp",EDGE,"E16");var subQ16=makeQuery(id+"F5.boolean.opBoolean","MERGE",EDGE,{"derivedFrom":[makeQuery(id+"F4.opExtrude","SWEPT_EDGE",EDGE,{"disambiguationData":[OSD([sQuery(id+"F3.wireOp",EDGE,"E17"),subQ3,subQ2])]}),makeQuery(id+"F5.opPattern","COPY",EDGE,{"derivedFrom":makeQuery(id+"F4.opExtrude","SWEPT_EDGE",EDGE,{"disambiguationData":[OSD([subQ15,sQuery(id+"F3.wireOp",EDGE,"E18"),subQ2])]}),"instanceName":"3"})]});Q27=qUnion([makeQuery(id+"F10.boolean.opBoolean","MERGE",EDGE,{"derivedFrom":[makeQuery(id+"F9.boolean.opBoolean","SPLIT",EDGE,{"disambiguationData":[TD([makeQuery(id+"F7.boolean.opBoolean","COPY",FACE,{"derivedFrom":makeQuery(id+"F7.opExtrude","SWEPT_FACE",FACE,{"disambiguationData":[OSD([sQuery(id+"F6.wireOp",EDGE,"E25")])]})})])],"derivedFrom":subQ16}),makeQuery(id+"F10.opLoft","SWEPT_EDGE",EDGE,{"disambiguationData":[OSD([subQ15,subQ2,subQ1,subQ0])]})]}),makeQuery(id+"F9.boolean.opBoolean","MERGE",EDGE,{"derivedFrom":[subQ16,makeQuery(id+"F9.opExtrude","SWEPT_EDGE",EDGE,{"disambiguationData":[OSD([subQ1,subQ0])]})]}),makeQuery(id+"F11.boolean.opBoolean","MERGE",EDGE,{"derivedFrom":[makeQuery(id+"F9.boolean.opBoolean","SPLIT",EDGE,{"disambiguationData":[TD([makeQuery(id+"F7.boolean.opBoolean","COPY",FACE,{"derivedFrom":makeQuery(id+"F7.opExtrude","SWEPT_FACE",FACE,{"disambiguationData":[OSD([sQuery(id+"F6.wireOp",EDGE,"E27")])]})})])],"derivedFrom":subQ16}),makeQuery(id+"F11.opLoft","SWEPT_EDGE",EDGE,{"disambiguationData":[OSD([subQ3,subQ2,subQ1,subQ0])]})]})]);}
            var Q28;
            Q28=makeQuery(id+"F5.opPattern","COPY",EDGE,{"derivedFrom":makeQuery(id+"F4.opExtrude","SWEPT_EDGE",EDGE,{"disambiguationData":[OSD([sQuery(id+"F3.wireOp",EDGE,"E17"),sQuery(id+"F3.wireOp",EDGE,"E19"),sQuery(id+"F3.wireOp",EDGE,"E20")])]}),"instanceName":"3"});
            var Q29;
            Q29=makeQuery(id+"F5.opPattern","COPY",EDGE,{"derivedFrom":makeQuery(id+"F4.opExtrude","SWEPT_EDGE",EDGE,{"disambiguationData":[OSD([sQuery(id+"F3.wireOp",EDGE,"E16"),sQuery(id+"F3.wireOp",EDGE,"E18"),sQuery(id+"F3.wireOp",EDGE,"E20")])]}),"instanceName":"2"});
            var Q30;
            Q30=makeQuery(id+"F5.opPattern","COPY",EDGE,{"derivedFrom":makeQuery(id+"F4.opExtrude","SWEPT_EDGE",EDGE,{"disambiguationData":[OSD([sQuery(id+"F3.wireOp",EDGE,"E17"),sQuery(id+"F3.wireOp",EDGE,"E19"),sQuery(id+"F3.wireOp",EDGE,"E20")])]}),"instanceName":"2"});
            var Q31;
            Q31=makeQuery(id+"F5.opPattern","COPY",EDGE,{"derivedFrom":makeQuery(id+"F4.opExtrude","SWEPT_EDGE",EDGE,{"disambiguationData":[OSD([sQuery(id+"F3.wireOp",EDGE,"E16"),sQuery(id+"F3.wireOp",EDGE,"E18"),sQuery(id+"F3.wireOp",EDGE,"E20")])]}),"instanceName":"1"});
            var Q32;
            Q32=makeQuery(id+"F5.opPattern","COPY",EDGE,{"derivedFrom":makeQuery(id+"F4.opExtrude","SWEPT_EDGE",EDGE,{"disambiguationData":[OSD([sQuery(id+"F3.wireOp",EDGE,"E17"),sQuery(id+"F3.wireOp",EDGE,"E19"),sQuery(id+"F3.wireOp",EDGE,"E20")])]}),"instanceName":"1"});
            var Q33;
            Q33=makeQuery(id+"F2.opSweep","SWEPT_EDGE",EDGE,{"disambiguationData":[OSD([sQuery(id+"F0.wireOp",EDGE,"E0.3"),sQuery(id+"F1.wireOp",EDGE,"E4"),sQuery(id+"F1.wireOp",EDGE,"E6"),sQuery(id+"F1.wireOp",EDGE,"E8")])]});
            var Q34;
            Q34=makeQuery(id+"F2.opSweep","SWEPT_EDGE",EDGE,{"disambiguationData":[OSD([sQuery(id+"F0.wireOp",EDGE,"E0.3"),sQuery(id+"F1.wireOp",EDGE,"E5"),sQuery(id+"F1.wireOp",EDGE,"E7"),sQuery(id+"F1.wireOp",EDGE,"E8"),sQuery(id+"F1.wireOp",EDGE,"E11")])]});
            var Q35;
            Q35=makeQuery(id+"F4.opExtrude","SWEPT_EDGE",EDGE,{"disambiguationData":[OSD([sQuery(id+"F3.wireOp",EDGE,"E16"),sQuery(id+"F3.wireOp",EDGE,"E18"),sQuery(id+"F3.wireOp",EDGE,"E20")])]});
            var Q36;
            Q36=makeQuery(id+"F2.opSweep","SWEPT_EDGE",EDGE,{"disambiguationData":[OSD([sQuery(id+"F0.wireOp",EDGE,"E0.4"),sQuery(id+"F1.wireOp",EDGE,"E4"),sQuery(id+"F1.wireOp",EDGE,"E6"),sQuery(id+"F1.wireOp",EDGE,"E8")])]});
            var Q37;
            Q37=makeQuery(id+"F2.opSweep","SWEPT_EDGE",EDGE,{"disambiguationData":[OSD([sQuery(id+"F0.wireOp",EDGE,"E0.4"),sQuery(id+"F1.wireOp",EDGE,"E5"),sQuery(id+"F1.wireOp",EDGE,"E7"),sQuery(id+"F1.wireOp",EDGE,"E8"),sQuery(id+"F1.wireOp",EDGE,"E11")])]});
            fillet(context, id + "F14", {"entities" : qUnion([Q0, Q1, Q2, Q3, Q4, Q5, Q6, Q7, Q8, Q9, Q10, Q11, Q12, Q13, Q14, Q15, Q16, Q17, Q18, Q19, Q20, Q21, Q22, Q23, Q24, Q25, Q26, Q27, Q28, Q29, Q30, Q31, Q32, Q33, Q34, Q35, Q36, Q37]), "radius" : 1.15 * mm, "allowEdgeOverflow" : false});
        }
    });
